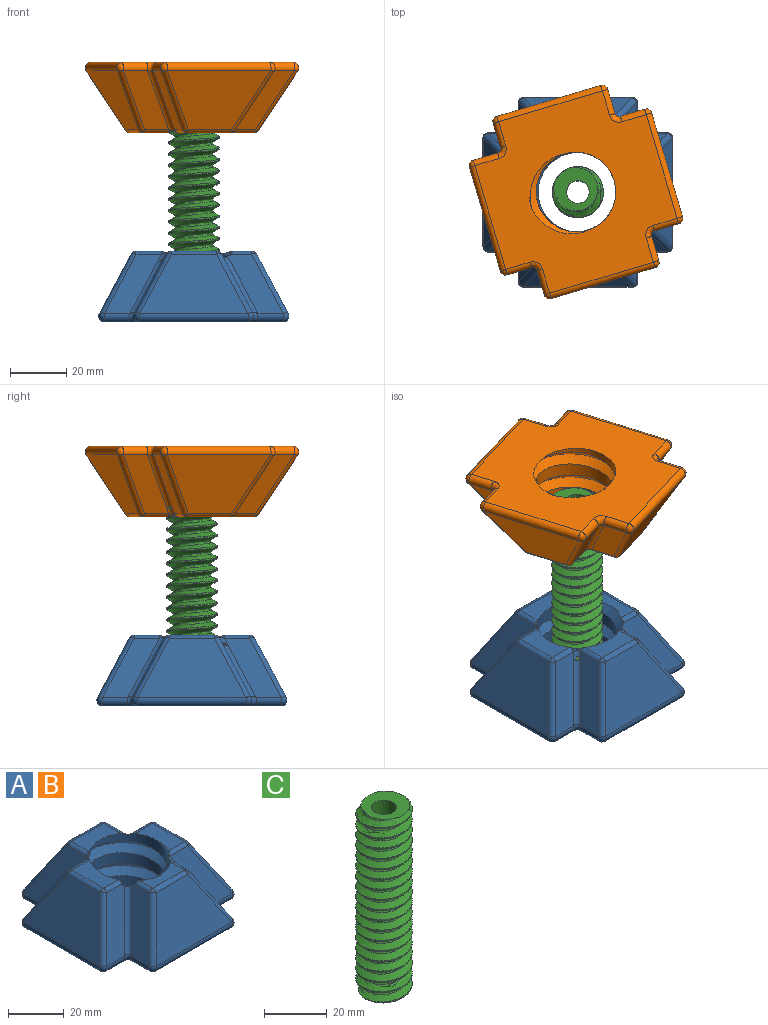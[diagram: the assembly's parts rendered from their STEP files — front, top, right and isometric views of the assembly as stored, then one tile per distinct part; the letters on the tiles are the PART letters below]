
ASSEMBLY  parts=3 mates=1
PART A: 81 faces, bbox 67.7x67.7x31.8 mm
  f0: bspline ~2.54x1.87mm, area 0.2mm2, adj f8,f57,f78
  f1: plane 16.09x7.02mm, normal (0,0,1), area 78.5mm2, adj f5,f8,f50,f78,f79
  f2: plane 16.32x9.21mm, normal (0,0,1), area 109.7mm2, adj f4,f6,f41,f77,f80
  f3: plane 16.01x8.9mm, normal (0,0,1), area 115.4mm2, adj f9,f12,f65,f77
  f4: cylinder r=2mm len=7.6mm, axis (-1,0,0), area 16.2mm2, adj f2,f18,f37,f80
  f5: cylinder r=2mm len=7.15mm, axis (0,-1,0), area 15.2mm2, adj f1,f19,f45,f78,f79
  f6: cylinder r=2mm len=8.97mm, axis (-1,0,0), area 19.4mm2, adj f2,f7,f16,f46,f77
  f7: bspline ~3.43x3.43mm, area 3.2mm2, adj f6,f9,f51,f77
  f8: cylinder r=2mm len=8.97mm, axis (0,-1,0), area 17.8mm2, adj f0,f1,f21,f54,f78
  f9: cylinder r=2mm len=8.97mm, axis (0,-1,0), area 19.4mm2, adj f3,f7,f15,f61,f77
  f10: bspline ~2.54x1.87mm, area 0.4mm2, adj f11,f57,f78
  f11: cylinder r=2mm len=8.97mm, axis (-1,0,0), area 18.7mm2, adj f10,f22,f27,f70,f78
  f12: cylinder r=2mm len=8.97mm, axis (0,-1,0), area 19.4mm2, adj f3,f13,f25,f71,f77
  f13: bspline ~3.43x3.43mm, area 3.2mm2, adj f12,f14,f75,f77
  f14: cylinder r=2mm len=8.97mm, axis (-1,0,0), area 19.4mm2, adj f13,f24,f27,f76,f77
  f15: plane 21x20.13mm, normal (-0.88,0,0.47), area 213.3mm2, adj f9,f51,f52,f58
  f16: plane 21x20.13mm, normal (0,0.88,0.47), area 213.3mm2, adj f6,f42,f43,f51
  f17: plane 38.34x21mm, normal (-0.88,0,0.47), area 646.4mm2, adj f34,f35,f41,f42
  f18: plane 21.03x19.63mm, normal (0,-0.88,0.47), area 212mm2, adj f4,f29,f33,f34,f78,f80
  f19: plane 21.04x19.7mm, normal (-0.88,0,0.47), area 212.4mm2, adj f5,f32,f33,f40,f78
  f20: plane 38.34x21mm, normal (0,-0.88,0.47), area 646.4mm2, adj f39,f40,f49,f50
  f21: plane 21x20.13mm, normal (0.88,0,0.47), area 213.3mm2, adj f8,f48,f49,f57
  f22: plane 21x20.13mm, normal (0,-0.88,0.47), area 213.3mm2, adj f11,f56,f57,f64
  f23: plane 38.34x21mm, normal (0.88,0,0.47), area 646.4mm2, adj f63,f64,f73,f74
  f24: plane 21x20.13mm, normal (0,0.88,0.47), area 213.3mm2, adj f14,f68,f73,f75
  f25: plane 21x20.13mm, normal (0.88,0,0.47), area 213.3mm2, adj f12,f66,f67,f75
  f26: plane 38.34x21mm, normal (0,0.88,0.47), area 646.4mm2, adj f58,f59,f65,f66
  f27: plane 16.23x9.12mm, normal (0,0,1), area 111.5mm2, adj f11,f14,f74,f77,f78
  f28: plane 63.34x63.34mm, normal (0,0,-1), area 2709.2mm2, adj f29,f30,f32,f35,f39,f43,f47,f48
  f29: cylinder r=2mm len=8.97mm, axis (1,0,0), area 36.9mm2, adj f18,f28,f30,f31
  f30: bspline ~3.53x3.53mm, area 14.4mm2, adj f28,f29,f32,f33
  f31: sphere r=2mm, area 9.2mm2, adj f29,f34,f35
  f32: cylinder r=2mm len=8.97mm, axis (0,1,0), area 36.9mm2, adj f19,f28,f30,f36
  f33: cylinder r=2mm len=20.38mm, axis (0.42,0.42,0.8), area 67.6mm2, adj f18,f19,f30,f78
  f34: cylinder r=2mm len=21.26mm, axis (-0.42,-0.42,-0.8), area 70.9mm2, adj f17,f18,f31,f37
  f35: cylinder r=2mm len=38.34mm, axis (0,1,0), area 157.9mm2, adj f17,f28,f31,f38
  f36: sphere r=2mm, area 9.2mm2, adj f32,f39,f40
  f37: sphere r=2mm, area 2.2mm2, adj f4,f34,f41
  f38: sphere r=2mm, area 9.2mm2, adj f35,f42,f43
  f39: cylinder r=2mm len=38.34mm, axis (1,0,0), area 157.9mm2, adj f20,f28,f36,f44
  f40: cylinder r=2mm len=21.26mm, axis (-0.42,-0.42,-0.8), area 70.9mm2, adj f19,f20,f36,f45
  f41: cylinder r=2mm len=16.01mm, axis (0,-1,0), area 34.7mm2, adj f2,f17,f37,f46
  f42: cylinder r=2mm len=21.26mm, axis (-0.42,0.42,-0.8), area 70.9mm2, adj f16,f17,f38,f46
  f43: cylinder r=2mm len=8.97mm, axis (1,0,0), area 36.9mm2, adj f16,f28,f38,f47
  f44: sphere r=2mm, area 9.8mm2, adj f39,f48,f49
  f45: sphere r=2mm, area 3.3mm2, adj f5,f40,f50
  f46: sphere r=2mm, area 5.6mm2, adj f6,f41,f42
  f47: bspline ~3.53x3.53mm, area 14.4mm2, adj f28,f43,f51,f52
  f48: cylinder r=2mm len=8.97mm, axis (0,1,0), area 36.9mm2, adj f21,f28,f44,f53
  f49: cylinder r=2mm len=21.26mm, axis (0.42,-0.42,-0.8), area 70.9mm2, adj f20,f21,f44,f54
  f50: cylinder r=2mm len=16.01mm, axis (-1,0,0), area 34.7mm2, adj f1,f20,f45,f54
  f51: cylinder r=2mm len=21.26mm, axis (0.42,-0.42,0.8), area 69.4mm2, adj f7,f15,f16,f47,f78,f80
  f52: cylinder r=2mm len=8.97mm, axis (0,1,0), area 36.9mm2, adj f15,f28,f47,f55
  f53: bspline ~3.53x3.53mm, area 14.4mm2, adj f28,f48,f56,f57
  f54: sphere r=2mm, area 2.8mm2, adj f8,f49,f50
  f55: sphere r=2mm, area 9.2mm2, adj f52,f58,f59
  f56: cylinder r=2mm len=8.97mm, axis (1,0,0), area 36.9mm2, adj f22,f28,f53,f60
  f57: cylinder r=2mm len=21.7mm, axis (-0.42,0.42,0.8), area 70.7mm2, adj f0,f10,f21,f22,f53,f78
  f58: cylinder r=2mm len=21.26mm, axis (-0.42,0.42,-0.8), area 70.9mm2, adj f15,f26,f55,f61
  f59: cylinder r=2mm len=38.34mm, axis (1,0,0), area 157.9mm2, adj f26,f28,f55,f62
  f60: sphere r=2mm, area 9.8mm2, adj f56,f63,f64
  f61: sphere r=2mm, area 3.3mm2, adj f9,f58,f65
  f62: sphere r=2mm, area 9.8mm2, adj f59,f66,f67
  f63: cylinder r=2mm len=38.34mm, axis (0,1,0), area 157.9mm2, adj f23,f28,f60,f69
  f64: cylinder r=2mm len=21.26mm, axis (0.42,-0.42,-0.8), area 70.9mm2, adj f22,f23,f60,f70
  f65: cylinder r=2mm len=16.01mm, axis (-1,0,0), area 34.7mm2, adj f3,f26,f61,f71
  f66: cylinder r=2mm len=21.26mm, axis (0.42,0.42,-0.8), area 70.9mm2, adj f25,f26,f62,f71
  f67: cylinder r=2mm len=8.97mm, axis (0,1,0), area 36.9mm2, adj f25,f28,f62,f72
  f68: cylinder r=2mm len=8.97mm, axis (1,0,0), area 36.9mm2, adj f24,f28,f69,f72
  f69: sphere r=2mm, area 9.8mm2, adj f63,f68,f73
  f70: sphere r=2mm, area 2.8mm2, adj f11,f64,f74
  f71: sphere r=2mm, area 4.5mm2, adj f12,f65,f66
  f72: bspline ~3.53x3.53mm, area 14.4mm2, adj f28,f67,f68,f75
  f73: cylinder r=2mm len=21.26mm, axis (0.42,0.42,-0.8), area 70.9mm2, adj f23,f24,f69,f76
  f74: cylinder r=2mm len=16.01mm, axis (0,-1,0), area 34.7mm2, adj f23,f27,f70,f76
  f75: cylinder r=2mm len=21.26mm, axis (-0.42,-0.42,0.8), area 70.9mm2, adj f13,f24,f25,f72
  f76: sphere r=2mm, area 1.6mm2, adj f14,f73,f74
  f77: cylinder r=14.1mm len=28.2mm, axis (0,0,-1), area 1057.8mm2, adj f2,f3,f6,f7,f9,f12,f13,f14
  f78: bspline ~33.4x33.4mm, area 881.1mm2, adj f0,f1,f5,f8,f10,f11,f18,f19
  f79: bspline ~11.81x6.73mm, area 4.8mm2, adj f1,f5,f78
  f80: bspline ~33.4x33.4mm, area 876.9mm2, adj f2,f4,f18,f28,f51,f77,f78
PART B: same geometry as A
PART C: 7 faces, bbox 19.1x21.9x74.4 mm
  f0: cylinder r=4mm len=70mm, axis (0,0,-1), area 1759.3mm2, adj f2,f3
  f1: cylinder r=9mm len=70mm, axis (0,0,-1), area 716.6mm2, adj f2,f3,f5,f6
  f2: plane 16.76x16.66mm, normal (0,0,1), area 140.5mm2, adj f0,f1,f4,f5,f6
  f3: plane 16.76x16.66mm, normal (0,0,-1), area 140.5mm2, adj f0,f1,f4,f5,f6
  f4: bspline ~73x15.78mm, area 827mm2, adj f2,f3,f5,f6
  f5: bspline ~73.25x20.78mm, area 2180.8mm2, adj f1,f2,f3,f4
  f6: bspline ~72.58x20.78mm, area 2176.5mm2, adj f1,f2,f3,f4
PLACE A rot(axis=(0,0,1),90deg) t=(0.67,0.03,16.46)mm
PLACE B rot(axis=(0.8,-0.6,0),180deg) t=(0,0,108.38)mm
PLACE C rot(axis=(0,0,1),106.6deg) t=(0.67,0.03,25.27)mm
MATE cylindrical C.f0 <-> A.f77  axis (0,0,-1) through (0.67,0.03,25.27)mm
